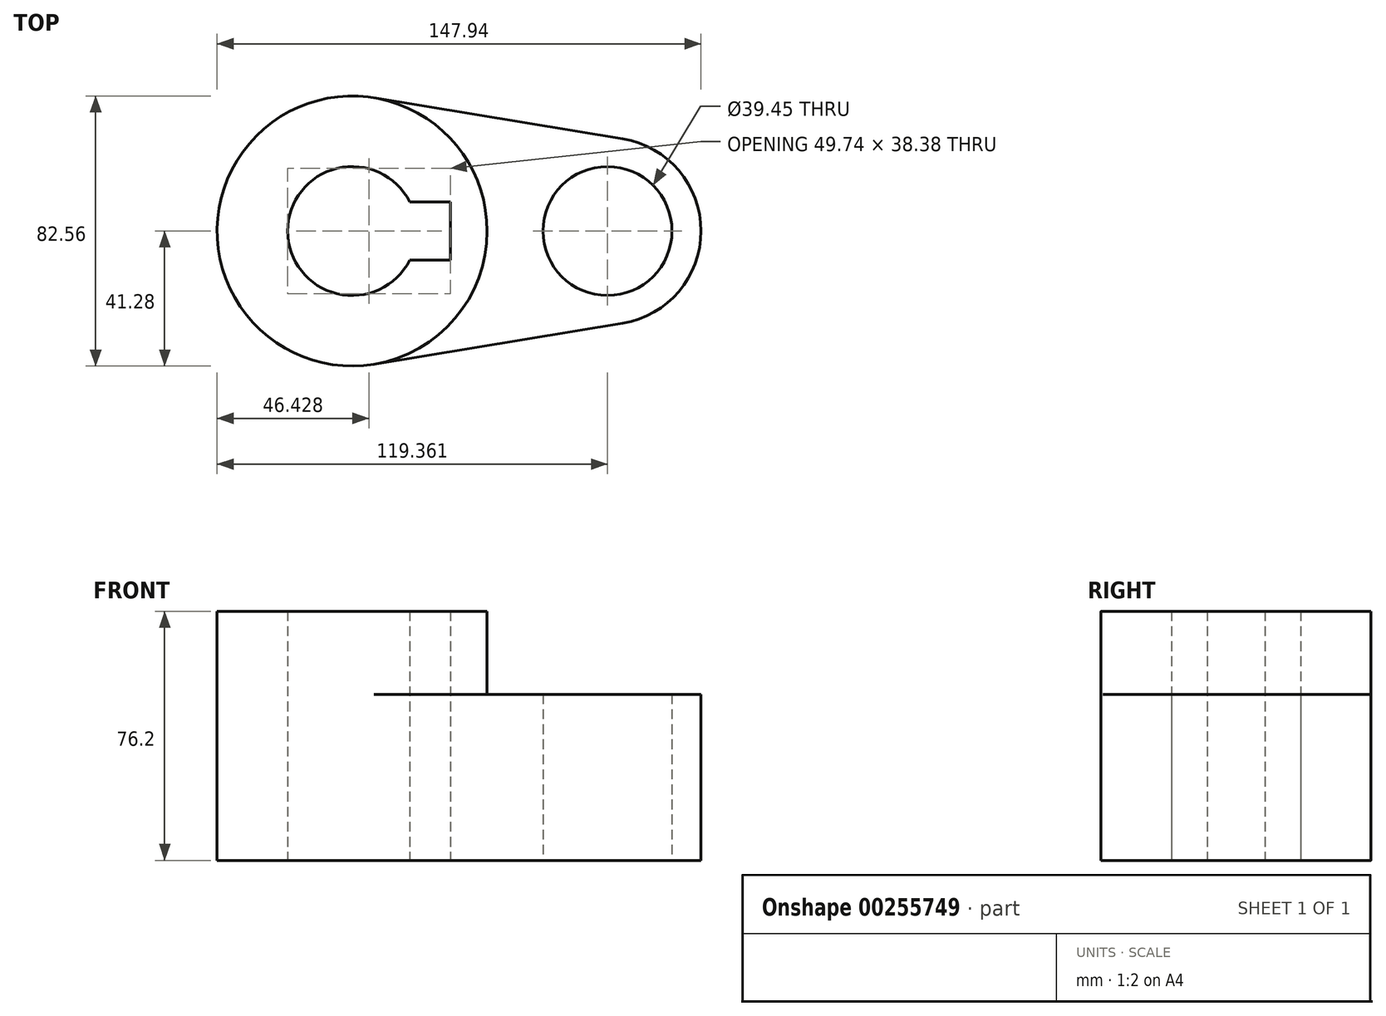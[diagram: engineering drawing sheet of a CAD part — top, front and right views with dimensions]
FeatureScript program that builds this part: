
annotation { "Feature Type Name" : "Feature", "Feature Type Description" : "" }
export const myFeature = defineFeature(function(context is Context, id is Id, definition is map)
    precondition{}
    {
        {
            var Q0;
            Q0=qCreatedBy(makeId("Top.planeOp"),FACE);
            var sketch = newSketch(context, id + "F0", { "sketchPlane" : qUnion([Q0])});
            skCircle(sketch, "E0", {"center": v(0, 0) * mm, "radius": 41.28 * mm});
            skCircle(sketch, "E1", {"center": v(78.08, 0) * mm, "radius": 28.58 * mm});
            skLineSegment(sketch, "E2", {"start": v(6.71, 40.73) * mm, "end": v(82.73, 28.2) * mm});
            skLineSegment(sketch, "E3", {"start": v(6.71, -40.73) * mm, "end": v(82.73, -28.2) * mm});
            skCircle(sketch, "E4", {"center": v(0, 0) * mm, "radius": 19.72 * mm});
            skCircle(sketch, "E5", {"center": v(78.08, 0) * mm, "radius": 19.72 * mm});
            skLineSegment(sketch, "E6.bottom", {"start": v(-30.02, 8.87) * mm, "end": v(30.02, 8.87) * mm});
            skLineSegment(sketch, "E6.top", {"start": v(-30.02, -8.87) * mm, "end": v(30.02, -8.87) * mm});
            skLineSegment(sketch, "E6.left", {"start": v(-30.02, 8.87) * mm, "end": v(-30.02, -8.87) * mm});
            skLineSegment(sketch, "E6.right", {"start": v(30.02, 8.87) * mm, "end": v(30.02, -8.87) * mm});
            skSolve(sketch);
        }
        {
            var Q0;
            {var subQ5=sQuery(id+"F0.wireOp",EDGE,"E6.left");Q0=makeQuery(id+"F0.imprint","IMPRINT",FACE,{"disambiguationData":[TD([[makeQuery(id+"F0.imprint","IMPRINT",EDGE,{"derivedFrom":subQ5}),1.0]])]});}
            var Q1;
            {var subQ11=sQuery(id+"F0.wireOp",EDGE,"E6.left");Q1=makeQuery(id+"F0.imprint","IMPRINT",FACE,{"disambiguationData":[TD([[makeQuery(id+"F0.imprint","IMPRINT",EDGE,{"derivedFrom":subQ11}),-1.0]])]});}
            var Q2;
            {var subQ0=sQuery(id+"F0.wireOp",EDGE,"E2");Q2=makeQuery(id+"F0.imprint","IMPRINT",FACE,{"disambiguationData":[TD([[makeQuery(id+"F0.imprint","IMPRINT",EDGE,{"derivedFrom":subQ0}),-1.0]])]});}
            var Q3;
            Q3=makeQuery(id+"F0.imprint","IMPRINT",FACE,{"disambiguationData":[TD([[makeQuery(id+"F0.imprint","IMPRINT",EDGE,{"derivedFrom":sQuery(id+"F0.wireOp",EDGE,"E5")}),-1.0]])]});
            extrude(context, id + "F1", {"entities" : qUnion([Q0, Q1, Q2, Q3]), "depth" : 50.8 * mm});
        }
        {
            var Q0;
            {var subQ11=sQuery(id+"F0.wireOp",EDGE,"E6.left");Q0=makeQuery(id+"F0.imprint","IMPRINT",FACE,{"disambiguationData":[TD([[makeQuery(id+"F0.imprint","IMPRINT",EDGE,{"derivedFrom":subQ11}),-1.0]])]});}
            var Q1;
            {var subQ5=sQuery(id+"F0.wireOp",EDGE,"E6.left");Q1=makeQuery(id+"F0.imprint","IMPRINT",FACE,{"disambiguationData":[TD([[makeQuery(id+"F0.imprint","IMPRINT",EDGE,{"derivedFrom":subQ5}),1.0]])]});}
            extrude(context, id + "F2", {"entities" : qUnion([Q0, Q1]), "operationType" : NewBodyOperationType.ADD, "depth" : 76.2 * mm});
        }
    });
